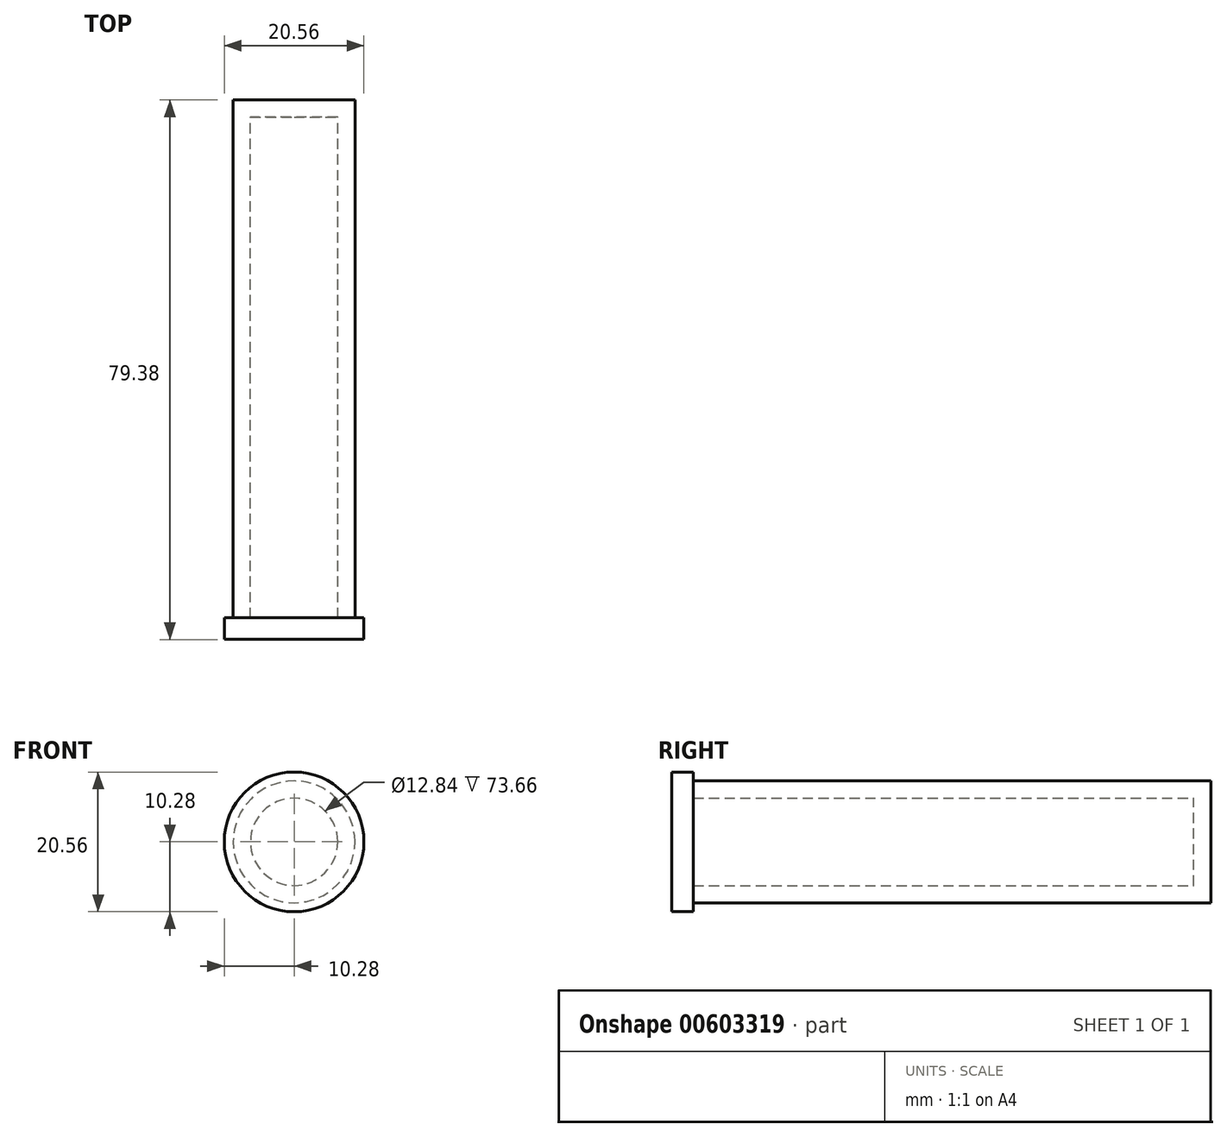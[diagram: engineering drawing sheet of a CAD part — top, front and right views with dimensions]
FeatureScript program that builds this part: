
annotation { "Feature Type Name" : "Feature", "Feature Type Description" : "" }
export const myFeature = defineFeature(function(context is Context, id is Id, definition is map)
    precondition{}
    {
        {
            var Q0;
            Q0=qCreatedBy(makeId("Front.planeOp"),FACE);
            var sketch = newSketch(context, id + "F0", { "sketchPlane" : qUnion([Q0])});
            skCircle(sketch, "E0", {"center": v(0, 0) * mm, "radius": 8.96 * mm});
            skSolve(sketch);
        }
        {
            var Q0;
            Q0 = qSketchRegion(id + "F0", true);
            extrude(context, id + "F1", {"entities" : qUnion([Q0]), "depth" : 13.72 * mm, "offsetDistance" : 25.4 * mm});
        }
        {
            var Q0;
            Q0 = qSketchRegion(id + "F0", true);
            extrude(context, id + "F2", {"entities" : qUnion([Q0]), "operationType" : NewBodyOperationType.ADD, "depth" : 76.2 * mm, "offsetDistance" : 25.4 * mm});
        }
        {
            var Q0;
            Q0=makeQuery(id+"F2.opExtrude","CAP_FACE",FACE,{"disambiguationData":[OSD([sQuery(id+"F0.wireOp",EDGE,"E0")])],"isStart":false});
            shell(context, id + "F3", {"entities" : qUnion([Q0]), "thickness" : 2.54 * mm});
        }
        {
            var Q0;
            Q0=makeQuery(id+"F2.opExtrude","CAP_FACE",FACE,{"disambiguationData":[OSD([sQuery(id+"F0.wireOp",EDGE,"E0")])],"isStart":false});
            var sketch = newSketch(context, id + "F4", { "sketchPlane" : qUnion([Q0])});
            skCircle(sketch, "E1", {"center": v(0, 0) * mm, "radius": 10.28 * mm});
            skSolve(sketch);
        }
        {
            var Q0;
            Q0 = qSketchRegion(id + "F4", true);
            extrude(context, id + "F5", {"entities" : qUnion([Q0]), "operationType" : NewBodyOperationType.ADD, "depth" : 3.17 * mm, "offsetDistance" : 25.4 * mm});
        }
    });
